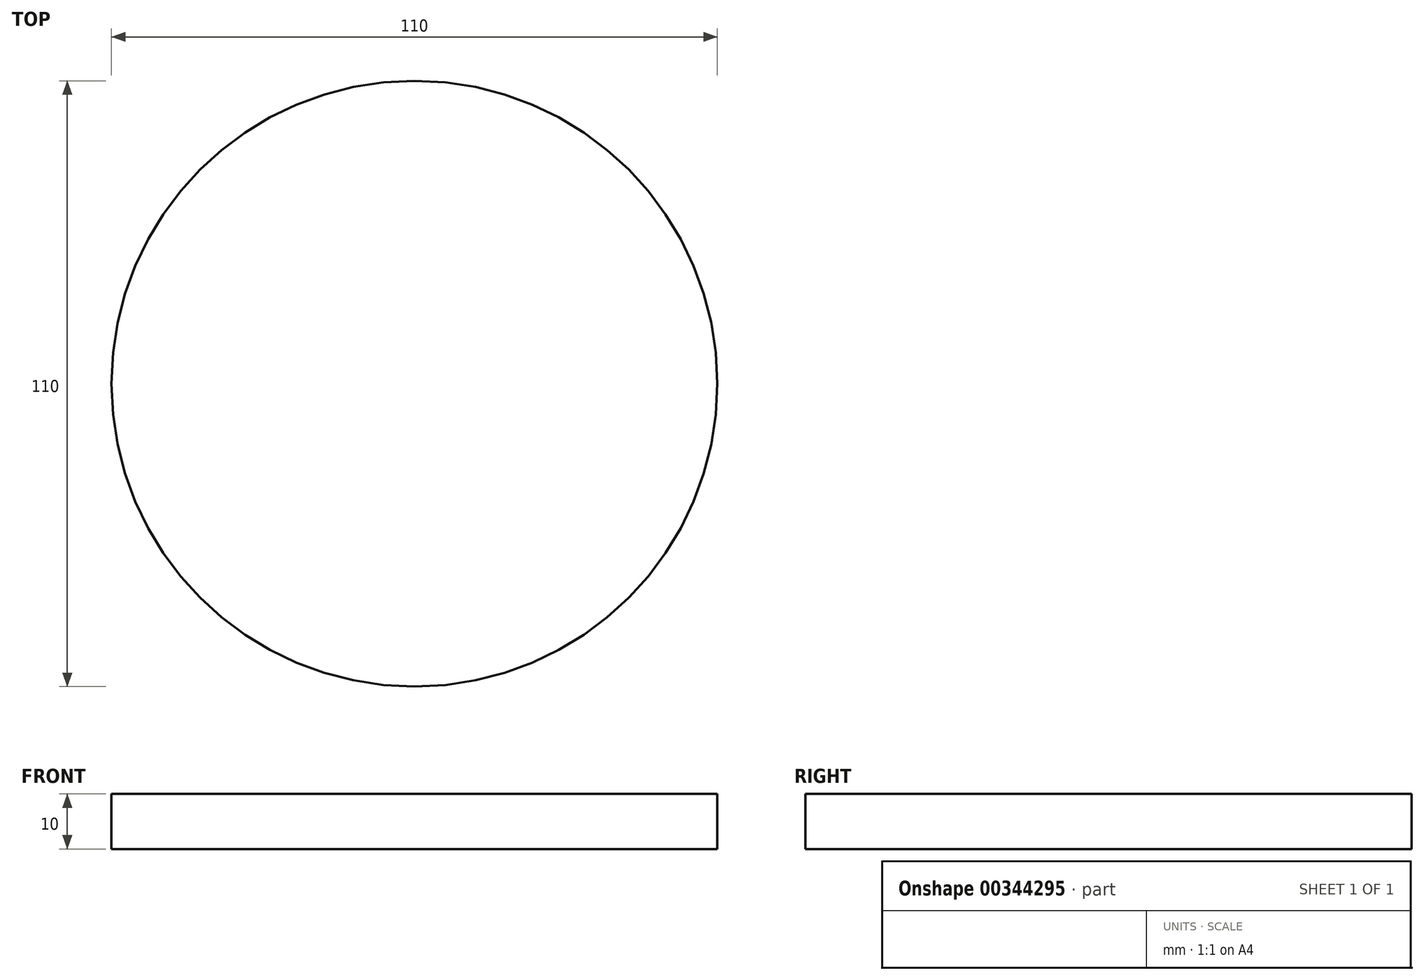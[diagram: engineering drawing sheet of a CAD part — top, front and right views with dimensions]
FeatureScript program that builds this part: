
annotation { "Feature Type Name" : "Feature", "Feature Type Description" : "" }
export const myFeature = defineFeature(function(context is Context, id is Id, definition is map)
    precondition{}
    {
        {
            var Q0;
            Q0=qCreatedBy(makeId("Top.planeOp"),FACE);
            var sketch = newSketch(context, id + "F0", { "sketchPlane" : qUnion([Q0])});
            skCircle(sketch, "E0", {"center": v(0, 0) * mm, "radius": 55 * mm});
            skSolve(sketch);
        }
        {
            var Q0;
            Q0=makeQuery(id+"F0.imprint","IMPRINT",FACE,{"disambiguationData":[TD([[makeQuery(id+"F0.imprint","IMPRINT",EDGE,{"derivedFrom":sQuery(id+"F0.wireOp",EDGE,"E0")}),1.0]])]});
            extrude(context, id + "F1", {"entities" : qUnion([Q0]), "depth" : 10 * mm});
        }
    });
